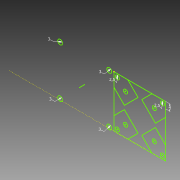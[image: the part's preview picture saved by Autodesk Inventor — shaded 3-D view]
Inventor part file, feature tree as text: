
AUTODESK INVENTOR PART (.ipt)
format: ipt  version: 2015 (Build 190159000, 159)  size: 95,232 bytes
history: native  units: mm
features: sketch x1
ambient origin geometry x8: Origin, YZ Plane, XZ Plane, XY Plane, X Axis, Y Axis, Z Axis, Center Point
feature tree (1):
  sketch  "Sketch1"  dims[d8=4.0mm d10=2.5mm d11=2.5mm d50=3.0mm d55=3.0mm d56=3.0mm d57=3.0mm]
